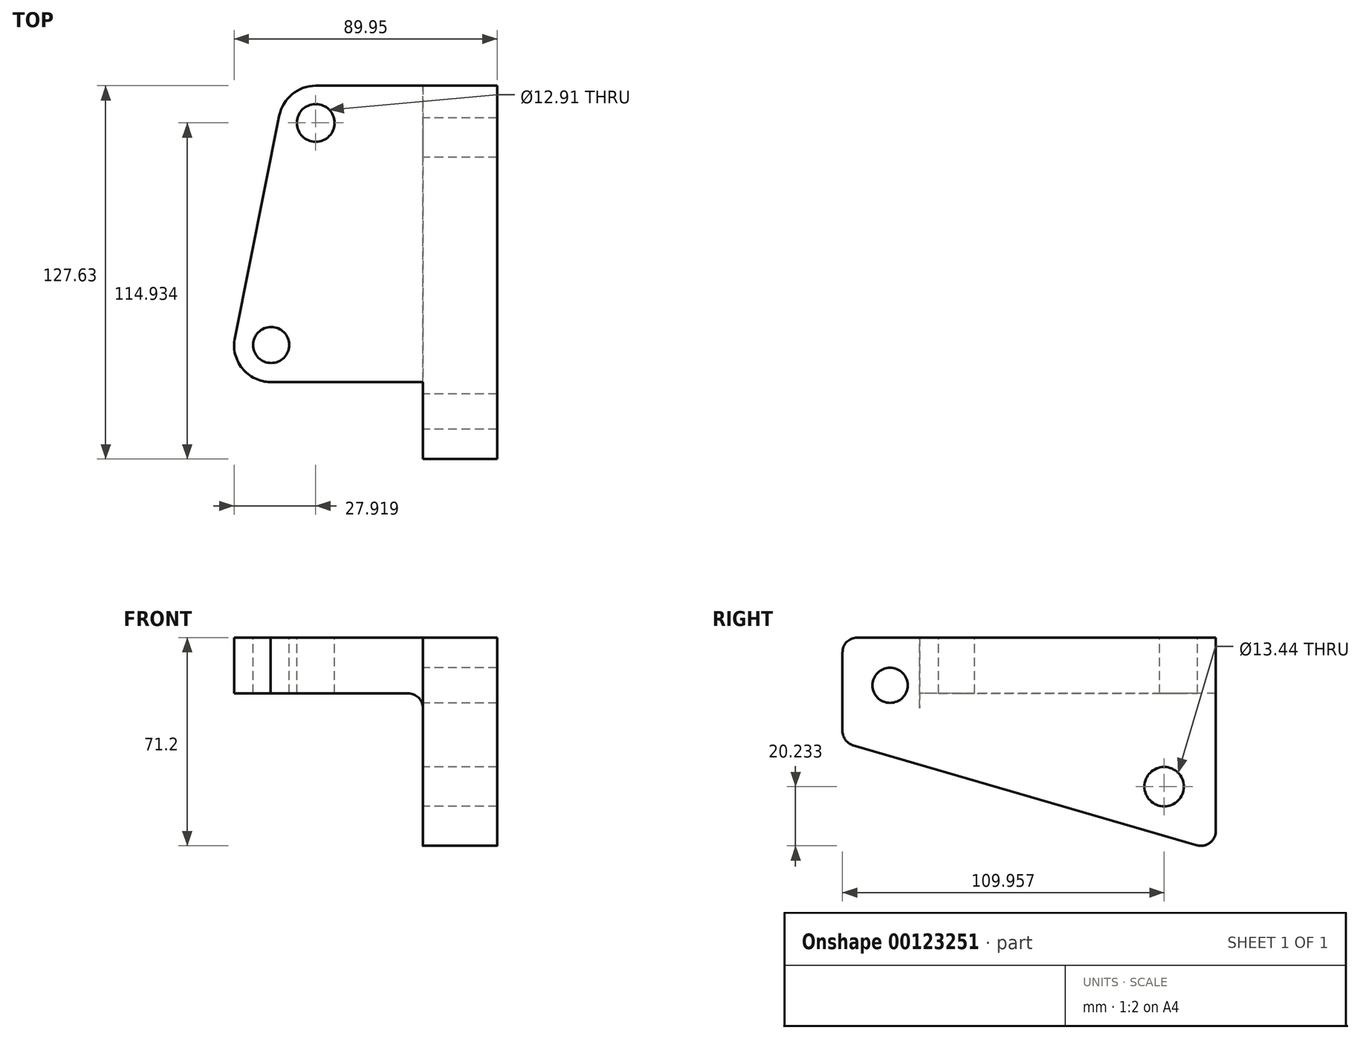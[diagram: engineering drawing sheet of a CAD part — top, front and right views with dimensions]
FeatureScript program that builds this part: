
annotation { "Feature Type Name" : "Feature", "Feature Type Description" : "" }
export const myFeature = defineFeature(function(context is Context, id is Id, definition is map)
    precondition{}
    {
        {
            var Q0;
            Q0=qCreatedBy(makeId("Right.planeOp"),FACE);
            var sketch = newSketch(context, id + "F0", { "sketchPlane" : qUnion([Q0])});
            skLineSegment(sketch, "E0", {"start": v(-63.5, 0) * mm, "end": v(-63.5, -35.76) * mm});
            skLineSegment(sketch, "E1", {"start": v(-63.5, -35.76) * mm, "end": v(64.13, -72.89) * mm});
            skLineSegment(sketch, "E2", {"start": v(64.13, -72.89) * mm, "end": v(64.13, 0) * mm});
            skLineSegment(sketch, "E3", {"start": v(64.13, 0) * mm, "end": v(-63.5, 0) * mm});
            skLineSegment(sketch, "E4", {"start": v(-29.2, 0) * mm, "end": v(-29.2, -25.16) * mm});
            skLineSegment(sketch, "E5", {"start": v(-29.2, -25.16) * mm, "end": v(64.13, -25.16) * mm});
            skLineSegment(sketch, "E6", {"start": v(64.13, -25.16) * mm, "end": v(64.13, 0) * mm});
            skCircle(sketch, "E7", {"center": v(-47.23, -16.32) * mm, "radius": 6.02 * mm});
            skCircle(sketch, "E8", {"center": v(46.46, -50.97) * mm, "radius": 6.72 * mm});
            skSolve(sketch);
        }
        {
            var Q0;
            Q0 = qSketchRegion(id + "F0", true);
            extrude(context, id + "F1", {"entities" : qUnion([Q0]), "depth" : 25.4 * mm});
        }
        {
            var Q0;
            Q0=qCreatedBy(makeId("Top.planeOp"),FACE);
            var sketch = newSketch(context, id + "F2", { "sketchPlane" : qUnion([Q0])});
            skLineSegment(sketch, "E9", {"start": v(-64.3, -21.99) * mm, "end": v(-49.08, 53.93) * mm});
            skPoint(sketch, "E10.visualSharp", {"position": v(-67.3, -36.95) * mm});
            skArc(sketch, "E10.filletArc", {"start": v(-64.3, -21.99) * mm, "mid": v(-61.74, -32.46) * mm, "end": v(-52.05, -37.18) * mm});
            skPoint(sketch, "E11.visualSharp", {"position": v(-47, 64.3) * mm});
            skArc(sketch, "E11.filletArc", {"start": v(-36.63, 64.13) * mm, "mid": v(-44.68, 61.26) * mm, "end": v(-49.08, 53.93) * mm});
            skLineSegment(sketch, "E12", {"start": v(-52.05, -37.18) * mm, "end": v(25.4, -37.18) * mm});
            skLineSegment(sketch, "E13", {"start": v(25.4, -37.18) * mm, "end": v(25.4, 64.13) * mm});
            skLineSegment(sketch, "E14", {"start": v(-36.63, 64.13) * mm, "end": v(25.4, 64.13) * mm});
            skCircle(sketch, "E15", {"center": v(-36.63, 51.43) * mm, "radius": 6.46 * mm});
            skCircle(sketch, "E16", {"center": v(-51.85, -24.49) * mm, "radius": 6.16 * mm});
            skSolve(sketch);
        }
        {
            var Q0;
            Q0 = qSketchRegion(id + "F2", true);
            extrude(context, id + "F3", {"entities" : qUnion([Q0]), "operationType" : NewBodyOperationType.ADD, "oppositeDirection" : true, "depth" : 19.05 * mm});
        }
        {
            var Q0;
            Q0=makeQuery(id+"F1.opExtrude","SWEPT_EDGE",EDGE,{"disambiguationData":[OSD([sQuery(id+"F0.wireOp",EDGE,"E1"),sQuery(id+"F0.wireOp",EDGE,"E2")])]});
            var Q1;
            Q1=makeQuery(id+"F1.opExtrude","SWEPT_EDGE",EDGE,{"disambiguationData":[OSD([sQuery(id+"F0.wireOp",EDGE,"E0"),sQuery(id+"F0.wireOp",EDGE,"E1")])]});
            var Q2;
            Q2=makeQuery(id+"F1.opExtrude","SWEPT_EDGE",EDGE,{"disambiguationData":[OSD([sQuery(id+"F0.wireOp",EDGE,"E0"),sQuery(id+"F0.wireOp",EDGE,"E3")])]});
            var Q3;
            Q3=makeQuery(id+"F3.boolean.opBoolean","INTERSECT",EDGE,{"derivedFrom":[makeQuery(id+"F1.opExtrude","CAP_FACE",FACE,{"disambiguationData":[OSD([sQuery(id+"F0.wireOp",EDGE,"E0"),sQuery(id+"F0.wireOp",EDGE,"E1"),sQuery(id+"F0.wireOp",EDGE,"E2"),sQuery(id+"F0.wireOp",EDGE,"E3"),sQuery(id+"F0.wireOp",EDGE,"E6"),sQuery(id+"F0.wireOp",EDGE,"E7"),sQuery(id+"F0.wireOp",EDGE,"E8")])],"isStart":true}),makeQuery(id+"F3.opExtrude","CAP_FACE",FACE,{"disambiguationData":[OSD([sQuery(id+"F2.wireOp",EDGE,"E9"),sQuery(id+"F2.wireOp",EDGE,"E10.filletArc"),sQuery(id+"F2.wireOp",EDGE,"E11.filletArc"),sQuery(id+"F2.wireOp",EDGE,"E12"),sQuery(id+"F2.wireOp",EDGE,"E13"),sQuery(id+"F2.wireOp",EDGE,"E14")])],"isStart":false})]});
            fillet(context, id + "F4", {"entities" : qUnion([Q0, Q1, Q2, Q3]), "radius" : 5.08 * mm, "tangentPropagation" : true, "allowEdgeOverflow" : false});
        }
    });
